# Revit family: HERZ Ball valve with lever hold and extended spindle (DZR) 2190
name_source: partatom
category: Rohrzubehör
revit_build: Autodesk Revit 2018 (Build: 20190510_1515(x64)
units: mm (PartAtom-declared; Revit-internal decimal feet)

## family parameters
Arbeitsebenenbasiert = Nein
Beim Laden mit Abzugskörper schneiden = Nein
Bemaßung runder Anschluss = Durchmesser verwenden
Gemeinsam genutzt = Nein
Immer vertikal = Ja
OmniClass-Nummer = 23.65.55.14
OmniClass-Titel = Valves for Liquid Services
Teiletyp = Unterbricht

## types (1)
- HERZ Ball valve with lever hold and extended spindle (DZR) 2190
    Application = HERZ ball valve with extended spindle DZR is designed for building services such as heating or chilled water plants.
The operating conditions (temperature, pressure) should be constant.
Extended spindle allows easy installation of thicker insulation.
The handle is isolated seperately so that the valve can be opened and closed without breaking or damaging the insulation.
HERZ ball valve with extended spindle DZR is made from CW602N; this material has DZR properties (dezinfication resistant brass).
The ball valve is bi-directional, that means it allows flow of the medium in both directions.
    Ball = forged brass acc. to EN 12165, hollow, full bore, hard chrome plated, CW602N, DZR
    Ball seals = PTFE
    Body = forged brass acc. to EN 12165, nickel plated, CW602N DZR
    Field of application = HERZ ball valves have to be used as shut off elements.
Field of application are building services, such as heating or chilled water plants.
Ball valves are used wherever the medium flow has to be reliably closed.
Ball valve should not be used as regulating element so it has to be fully opened or fully closed (the handle should not be in intermediate position).
    Handle = lever handle, red, sheet steel - plated
    Hersteller = HERZ Armaturen Ges.m.b.H
    Internal threaded connectors = according to ISO 228
    Max. operating pressure = 2500000.0 Pa
    Max. operating temperature = 130 °C
    Max. operating temperature (water - no steam) = 110 °C
    Max. short-term temperature load = 150 °C
    Medium = Heating water quality according to ÖNORM H5195 or VDI-Standard 2035.
The use of ethylene or propylene glycol in a mixing ratio 25- 50% is allowed.
    Min. operating temperature = -10 °C
    Min. operating temperature (water) = 1 °C
    Min. short-term temperature load = -50 °C
    SCRNCODE = 05;10;02
    SCRNSEQ = ARM;ARM_TYP="ABVS";2
    Spindle = machined brass according to EN 12164, CW614N
    Spindle seals = EPDM
    URL = www.herzvalves.com
    W01 = 135.00°
